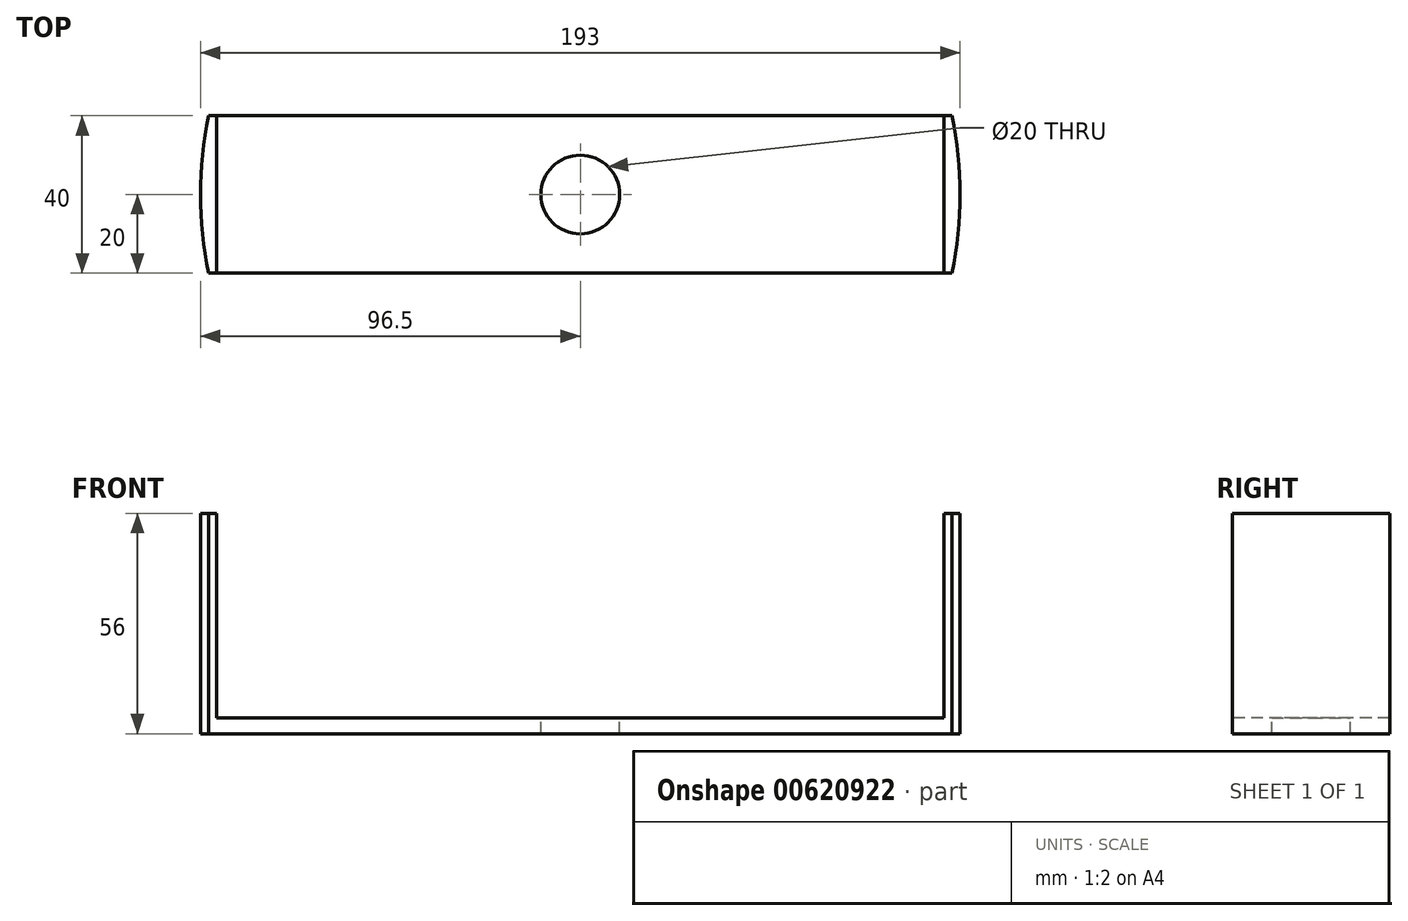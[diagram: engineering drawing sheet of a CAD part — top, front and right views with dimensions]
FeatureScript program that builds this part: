
annotation { "Feature Type Name" : "Feature", "Feature Type Description" : "" }
export const myFeature = defineFeature(function(context is Context, id is Id, definition is map)
    precondition{}
    {
        {
            var Q0;
            Q0=qCreatedBy(makeId("Top.planeOp"),FACE);
            var sketch = newSketch(context, id + "F0", { "sketchPlane" : qUnion([Q0])});
            skCircle(sketch, "E0", {"center": v(0, 0) * mm, "radius": 96.5 * mm});
            skLineSegment(sketch, "E1", {"start": v(0, 0) * mm, "end": v(0, 20) * mm, "construction": true});
            skLineSegment(sketch, "E2", {"start": v(0, 20) * mm, "end": v(0, -20) * mm, "construction": true});
            skLineSegment(sketch, "E3", {"start": v(0, 20) * mm, "end": v(-94.4, 20) * mm});
            skLineSegment(sketch, "E4", {"start": v(0, -20) * mm, "end": v(-94.4, -20) * mm});
            skLineSegment(sketch, "E5", {"start": v(0, 20) * mm, "end": v(94.4, 20) * mm});
            skLineSegment(sketch, "E6", {"start": v(0, -20) * mm, "end": v(94.4, -20) * mm});
            skSolve(sketch);
        }
        {
            var Q0;
            {var subQ1=sQuery(id+"F0.wireOp",EDGE,"E3");Q0=makeQuery(id+"F0.imprint","IMPRINT",FACE,{"disambiguationData":[TD([[makeQuery(id+"F0.imprint","IMPRINT",EDGE,{"derivedFrom":subQ1}),1.0]])]});}
            extrude(context, id + "F1", {"entities" : qUnion([Q0]), "depth" : 56 * mm, "offsetDistance" : 25 * mm});
        }
        {
            var Q0;
            Q0=makeQuery(id+"F1.opExtrude","CAP_FACE",FACE,{"disambiguationData":[OSD([sQuery(id+"F0.wireOp",EDGE,"E0"),sQuery(id+"F0.wireOp",EDGE,"E3"),sQuery(id+"F0.wireOp",EDGE,"E4"),sQuery(id+"F0.wireOp",EDGE,"E5"),sQuery(id+"F0.wireOp",EDGE,"E6")])],"isStart":false});
            var sketch = newSketch(context, id + "F2", { "sketchPlane" : qUnion([Q0])});
            skLineSegment(sketch, "E7", {"start": v(-94.4, 20) * mm, "end": v(-92.4, 20) * mm});
            skLineSegment(sketch, "E8", {"start": v(-92.4, 20) * mm, "end": v(-92.4, -20) * mm});
            skLineSegment(sketch, "E9", {"start": v(94.4, -20) * mm, "end": v(92.4, -20) * mm});
            skLineSegment(sketch, "E10", {"start": v(92.4, -20) * mm, "end": v(92.4, 20) * mm});
            skCircle(sketch, "E11", {"center": v(0, 0) * mm, "radius": 10 * mm});
            skSolve(sketch);
        }
        {
            var Q0;
            {var subQ0=sQuery(id+"F2.wireOp",EDGE,"E8");Q0=makeQuery(id+"F2.imprint","IMPRINT",FACE,{"disambiguationData":[TD([[makeQuery(id+"F2.imprint","IMPRINT",EDGE,{"derivedFrom":subQ0}),1.0]])]});}
            extrude(context, id + "F3", {"entities" : qUnion([Q0]), "operationType" : NewBodyOperationType.REMOVE, "oppositeDirection" : true, "depth" : 52 * mm, "offsetDistance" : 25 * mm});
        }
        {
            var Q0;
            Q0=makeQuery(id+"F2.imprint","IMPRINT",FACE,{"disambiguationData":[TD([[makeQuery(id+"F2.imprint","IMPRINT",EDGE,{"derivedFrom":sQuery(id+"F2.wireOp",EDGE,"E11")}),1.0]])]});
            extrude(context, id + "F4", {"entities" : qUnion([Q0]), "operationType" : NewBodyOperationType.REMOVE, "oppositeDirection" : true, "depth" : 60 * mm, "offsetDistance" : 25 * mm});
        }
    });
